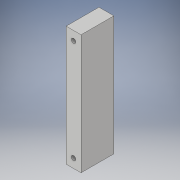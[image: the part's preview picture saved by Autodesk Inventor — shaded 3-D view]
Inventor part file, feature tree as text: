
AUTODESK INVENTOR PART (.ipt)
format: ipt  version: 2019 (Build 230136000, 136)  size: 104,960 bytes
history: native  units: mm
features: extrude x2, sketch x2, other x1
ambient origin geometry x8: Origin, YZ Plane, XZ Plane, XY Plane, X Axis, Y Axis, Z Axis, Center Point
bodies: Body1 (feature_tree)
feature tree (5):
  other  "Sólido1"
  extrude  "Extrusión1"  Depth=110.0mm
  extrude  "Extrusión2"  Depth=400.0mm
  sketch  "Boceto1"  dims[d0=50.0mm d1=110.0mm]
  sketch  "Boceto2"  dims[d2=400.0mm d3=0.0mm d4=30.0mm d5=30.0mm d6=15.0mm d7=15.0mm d8=0.0mm d9=0.0mm]
